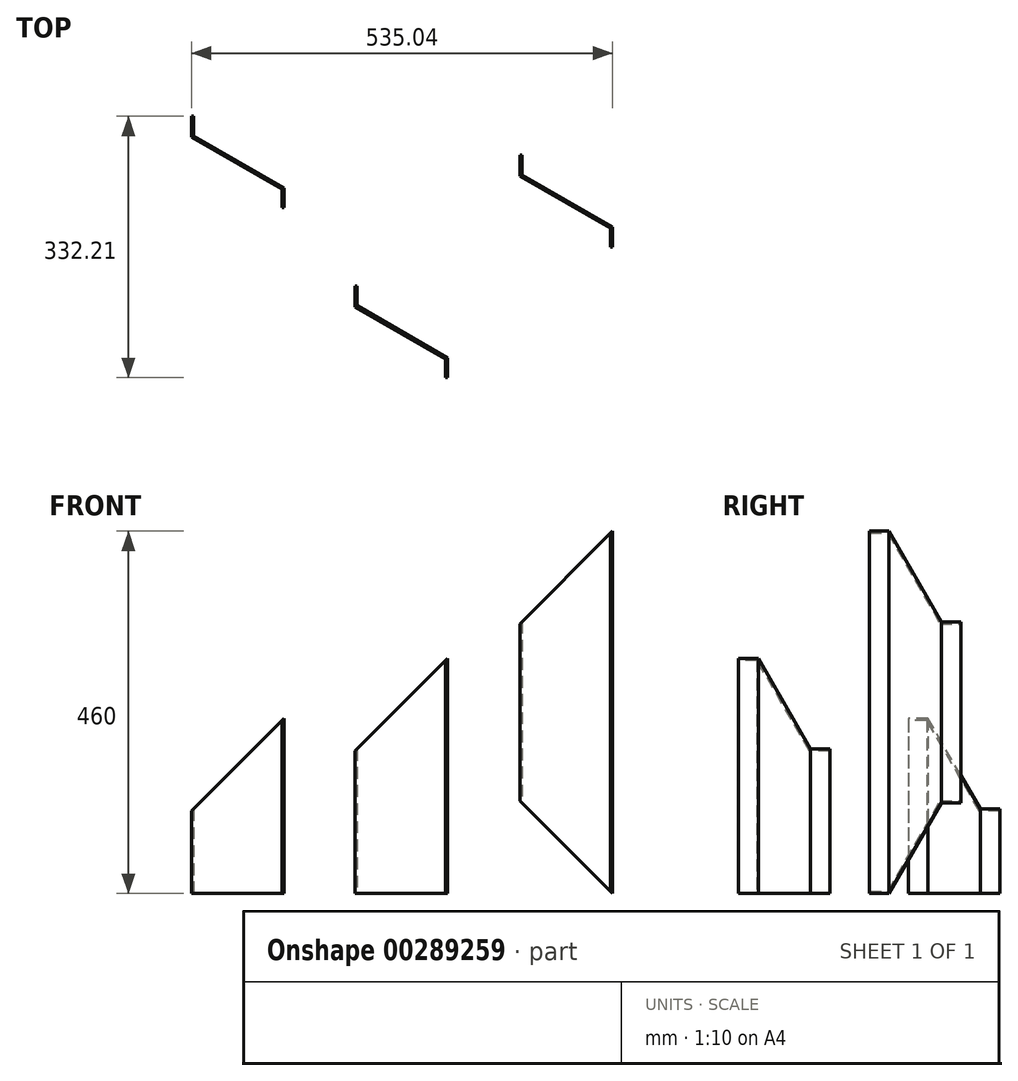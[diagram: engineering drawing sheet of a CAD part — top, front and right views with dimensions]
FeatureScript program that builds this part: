
annotation { "Feature Type Name" : "Feature", "Feature Type Description" : "" }
export const myFeature = defineFeature(function(context is Context, id is Id, definition is map)
    precondition{}
    {
        {
            var Q0;
            Q0=qCreatedBy(makeId("Top.planeOp"),FACE);
            var sketch = newSketch(context, id + "F0", { "sketchPlane" : qUnion([Q0])});
            skLineSegment(sketch, "E0", {"start": v(-174.05, 168.26) * mm, "end": v(-174.05, 143.26) * mm});
            skLineSegment(sketch, "E1", {"start": v(-174.05, 143.26) * mm, "end": v(-59.05, 76.86) * mm});
            skLineSegment(sketch, "E2", {"start": v(-59.05, 76.86) * mm, "end": v(-59.05, 51.86) * mm});
            skLineSegment(sketch, "E3", {"start": v(-174.05, 168.26) * mm, "end": v(-176.55, 168.26) * mm});
            skLineSegment(sketch, "E4", {"start": v(-176.55, 168.26) * mm, "end": v(-176.55, 141.82) * mm});
            skLineSegment(sketch, "E5", {"start": v(-176.55, 141.82) * mm, "end": v(-61.55, 75.42) * mm});
            skLineSegment(sketch, "E6", {"start": v(-61.55, 75.42) * mm, "end": v(-61.55, 51.86) * mm});
            skLineSegment(sketch, "E7", {"start": v(-61.55, 51.86) * mm, "end": v(-59.05, 51.86) * mm});
            skSolve(sketch);
        }
        {
            var Q0;
            Q0=makeQuery(id+"F0.imprint","IMPRINT",FACE,{"disambiguationData":[TD([[makeQuery(id+"F0.imprint","IMPRINT",EDGE,{"derivedFrom":sQuery(id+"F0.wireOp",EDGE,"E0")}),-1.0]])]});
            extrude(context, id + "F1", {"entities" : qUnion([Q0]), "depth" : 222 * mm});
        }
        {
            var Q0;
            Q0=makeQuery(id+"F1.opExtrude","SWEPT_FACE",FACE,{"disambiguationData":[OSD([sQuery(id+"F0.wireOp",EDGE,"E7")])]});
            var sketch = newSketch(context, id + "F2", { "sketchPlane" : qUnion([Q0])});
            skLineSegment(sketch, "E8.0", {"start": v(-176.55, 222) * mm, "end": v(-176.55, 0) * mm});
            skLineSegment(sketch, "E9.0", {"start": v(-176.55, 222) * mm, "end": v(-61.55, 222) * mm});
            skPoint(sketch, "E10.0", {"position": v(-59.05, 222) * mm});
            skLineSegment(sketch, "E11.0", {"start": v(-59.05, 222) * mm, "end": v(-59.05, 0) * mm});
            skLineSegment(sketch, "E12", {"start": v(-59.05, 222) * mm, "end": v(-176.55, 104.5) * mm});
            skSolve(sketch);
        }
        {
            var Q0;
            {var subQ0=sQuery(id+"F2.wireOp",EDGE,"E9.0");Q0=makeQuery(id+"F2.imprint","IMPRINT",FACE,{"disambiguationData":[TD([[makeQuery(id+"F2.imprint","IMPRINT",EDGE,{"derivedFrom":subQ0}),-1.0]])]});}
            var Q1;
            {var subQ1=sQuery(id+"F0.wireOp",EDGE,"E7");var subQ2=makeQuery(id+"F1.opExtrude","CAP_EDGE",EDGE,{"disambiguationData":[OSD([subQ1])],"isStart":false});Q1=makeQuery(id+"F2.imprint","IMPRINT",FACE,{"disambiguationData":[TD([[makeQuery(id+"F2.imprint","IMPRINT",EDGE,{"derivedFrom":subQ2}),-1.0]])]});}
            extrude(context, id + "F3", {"entities" : qUnion([Q0, Q1]), "operationType" : NewBodyOperationType.REMOVE, "endBound" : BoundingType.THROUGH_ALL, "oppositeDirection" : true, "depth" : 25 * mm});
        }
        {
            var Q0;
            Q0=qCreatedBy(makeId("Top.planeOp"),FACE);
            var sketch = newSketch(context, id + "F4", { "sketchPlane" : qUnion([Q0])});
            skLineSegment(sketch, "E13", {"start": v(34.07, -47.55) * mm, "end": v(34.07, -72.55) * mm});
            skLineSegment(sketch, "E14", {"start": v(34.07, -72.55) * mm, "end": v(149.07, -138.95) * mm});
            skLineSegment(sketch, "E15", {"start": v(149.07, -138.95) * mm, "end": v(149.07, -163.95) * mm});
            skLineSegment(sketch, "E16", {"start": v(34.07, -47.55) * mm, "end": v(31.57, -47.55) * mm});
            skLineSegment(sketch, "E17", {"start": v(31.57, -47.55) * mm, "end": v(31.57, -74) * mm});
            skLineSegment(sketch, "E18", {"start": v(31.57, -74) * mm, "end": v(146.57, -140.4) * mm});
            skLineSegment(sketch, "E19", {"start": v(146.57, -140.4) * mm, "end": v(146.57, -163.95) * mm});
            skLineSegment(sketch, "E20", {"start": v(146.57, -163.95) * mm, "end": v(149.07, -163.95) * mm});
            skSolve(sketch);
        }
        {
            var Q0;
            Q0=makeQuery(id+"F4.imprint","IMPRINT",FACE,{"disambiguationData":[TD([[makeQuery(id+"F4.imprint","IMPRINT",EDGE,{"derivedFrom":sQuery(id+"F4.wireOp",EDGE,"E13")}),-1.0]])]});
            extrude(context, id + "F5", {"entities" : qUnion([Q0]), "depth" : 181 * mm + 117 * mm / cos(45 * degree) - 48 * mm});
        }
        {
            var Q0;
            Q0=makeQuery(id+"F5.opExtrude","SWEPT_FACE",FACE,{"disambiguationData":[OSD([sQuery(id+"F4.wireOp",EDGE,"E20")])]});
            var sketch = newSketch(context, id + "F6", { "sketchPlane" : qUnion([Q0])});
            skLineSegment(sketch, "E21", {"start": v(149.07, 298.46) * mm, "end": v(31.57, 180.96) * mm});
            skLineSegment(sketch, "E22.0", {"start": v(31.57, 298.46) * mm, "end": v(31.57, 0) * mm});
            skLineSegment(sketch, "E23.0", {"start": v(31.57, 298.46) * mm, "end": v(146.57, 298.46) * mm});
            skLineSegment(sketch, "E24.0", {"start": v(146.57, 298.46) * mm, "end": v(149.07, 298.46) * mm});
            skSolve(sketch);
        }
        {
            var Q0;
            {var subQ0=sQuery(id+"F6.wireOp",EDGE,"E24.0");Q0=makeQuery(id+"F6.imprint","IMPRINT",FACE,{"disambiguationData":[TD([[makeQuery(id+"F6.imprint","IMPRINT",EDGE,{"derivedFrom":subQ0}),-1.0]])]});}
            var Q1;
            {var subQ5=sQuery(id+"F6.wireOp",EDGE,"E23.0");Q1=makeQuery(id+"F6.imprint","IMPRINT",FACE,{"disambiguationData":[TD([[makeQuery(id+"F6.imprint","IMPRINT",EDGE,{"derivedFrom":subQ5}),-1.0]])]});}
            extrude(context, id + "F7", {"entities" : qUnion([Q0, Q1]), "operationType" : NewBodyOperationType.REMOVE, "endBound" : BoundingType.THROUGH_ALL, "oppositeDirection" : true, "depth" : 25 * mm});
        }
        {
            var Q0;
            Q0=qCreatedBy(makeId("Top.planeOp"),FACE);
            var sketch = newSketch(context, id + "F8", { "sketchPlane" : qUnion([Q0])});
            skLineSegment(sketch, "E25", {"start": v(243.49, 118.7) * mm, "end": v(243.49, 93.7) * mm});
            skLineSegment(sketch, "E26", {"start": v(243.49, 93.7) * mm, "end": v(358.49, 27.31) * mm});
            skLineSegment(sketch, "E27", {"start": v(358.49, 27.31) * mm, "end": v(358.49, 2.31) * mm});
            skLineSegment(sketch, "E28", {"start": v(243.49, 118.7) * mm, "end": v(240.99, 118.7) * mm});
            skLineSegment(sketch, "E29", {"start": v(240.99, 118.7) * mm, "end": v(240.99, 92.26) * mm});
            skLineSegment(sketch, "E30", {"start": v(240.99, 92.26) * mm, "end": v(355.99, 25.87) * mm});
            skLineSegment(sketch, "E31", {"start": v(355.99, 25.87) * mm, "end": v(355.99, 2.31) * mm});
            skLineSegment(sketch, "E32", {"start": v(355.99, 2.31) * mm, "end": v(358.49, 2.31) * mm});
            skSolve(sketch);
        }
        {
            var Q0;
            Q0=makeQuery(id+"F8.imprint","IMPRINT",FACE,{"disambiguationData":[TD([[makeQuery(id+"F8.imprint","IMPRINT",EDGE,{"derivedFrom":sQuery(id+"F8.wireOp",EDGE,"E25")}),-1.0]])]});
            extrude(context, id + "F9", {"entities" : qUnion([Q0]), "depth" : 400 * mm + 60 * mm});
        }
        {
            var Q0;
            Q0=makeQuery(id+"F9.opExtrude","SWEPT_FACE",FACE,{"disambiguationData":[OSD([sQuery(id+"F8.wireOp",EDGE,"E28")])]});
            var sketch = newSketch(context, id + "F10", { "sketchPlane" : qUnion([Q0])});
            skLineSegment(sketch, "E33.0", {"start": v(-243.49, 460) * mm, "end": v(-358.49, 460) * mm});
            skLineSegment(sketch, "E34.0", {"start": v(-358.49, 460) * mm, "end": v(-358.49, 0) * mm});
            skLineSegment(sketch, "E35.0", {"start": v(-243.49, 460) * mm, "end": v(-240.99, 460) * mm});
            skLineSegment(sketch, "E36", {"start": v(-358.49, 460) * mm, "end": v(-240.99, 342.5) * mm});
            skSolve(sketch);
        }
        {
            var Q0;
            {var subQ0=sQuery(id+"F10.wireOp",EDGE,"E33.0");Q0=makeQuery(id+"F10.imprint","IMPRINT",FACE,{"disambiguationData":[TD([[makeQuery(id+"F10.imprint","IMPRINT",EDGE,{"derivedFrom":subQ0}),1.0]])]});}
            var Q1;
            {var subQ0=sQuery(id+"F10.wireOp",EDGE,"E35.0");Q1=makeQuery(id+"F10.imprint","IMPRINT",FACE,{"disambiguationData":[TD([[makeQuery(id+"F10.imprint","IMPRINT",EDGE,{"derivedFrom":subQ0}),-1.0]])]});}
            extrude(context, id + "F11", {"entities" : qUnion([Q0, Q1]), "operationType" : NewBodyOperationType.REMOVE, "endBound" : BoundingType.THROUGH_ALL, "oppositeDirection" : true, "depth" : 25 * mm});
        }
        {
            var Q0;
            Q0=makeQuery(id+"F9.opExtrude","SWEPT_FACE",FACE,{"disambiguationData":[OSD([sQuery(id+"F8.wireOp",EDGE,"E28")])]});
            var sketch = newSketch(context, id + "F12", { "sketchPlane" : qUnion([Q0])});
            skLineSegment(sketch, "E37.0", {"start": v(-358.49, 460) * mm, "end": v(-358.49, 0) * mm});
            skLineSegment(sketch, "E38.0", {"start": v(-243.49, 0) * mm, "end": v(-358.49, 0) * mm});
            skLineSegment(sketch, "E39.0", {"start": v(-243.49, 0) * mm, "end": v(-240.99, 0) * mm});
            skLineSegment(sketch, "E40", {"start": v(-358.49, 0) * mm, "end": v(-240.99, 117.5) * mm});
            skSolve(sketch);
        }
        {
            var Q0;
            Q0 = qSketchRegion(id + "F12", true);
            var Q1;
            {var subQ0=sQuery(id+"F12.wireOp",EDGE,"E38.0");Q1=makeQuery(id+"F12.imprint","IMPRINT",FACE,{"disambiguationData":[TD([[makeQuery(id+"F12.imprint","IMPRINT",EDGE,{"derivedFrom":subQ0}),-1.0]])]});}
            var Q2;
            {var subQ0=sQuery(id+"F12.wireOp",EDGE,"E39.0");Q2=makeQuery(id+"F12.imprint","IMPRINT",FACE,{"disambiguationData":[TD([[makeQuery(id+"F12.imprint","IMPRINT",EDGE,{"derivedFrom":subQ0}),1.0]])]});}
            extrude(context, id + "F13", {"entities" : qUnion([Q0, Q1, Q2]), "operationType" : NewBodyOperationType.REMOVE, "endBound" : BoundingType.THROUGH_ALL, "oppositeDirection" : true, "depth" : 25 * mm});
        }
    });
